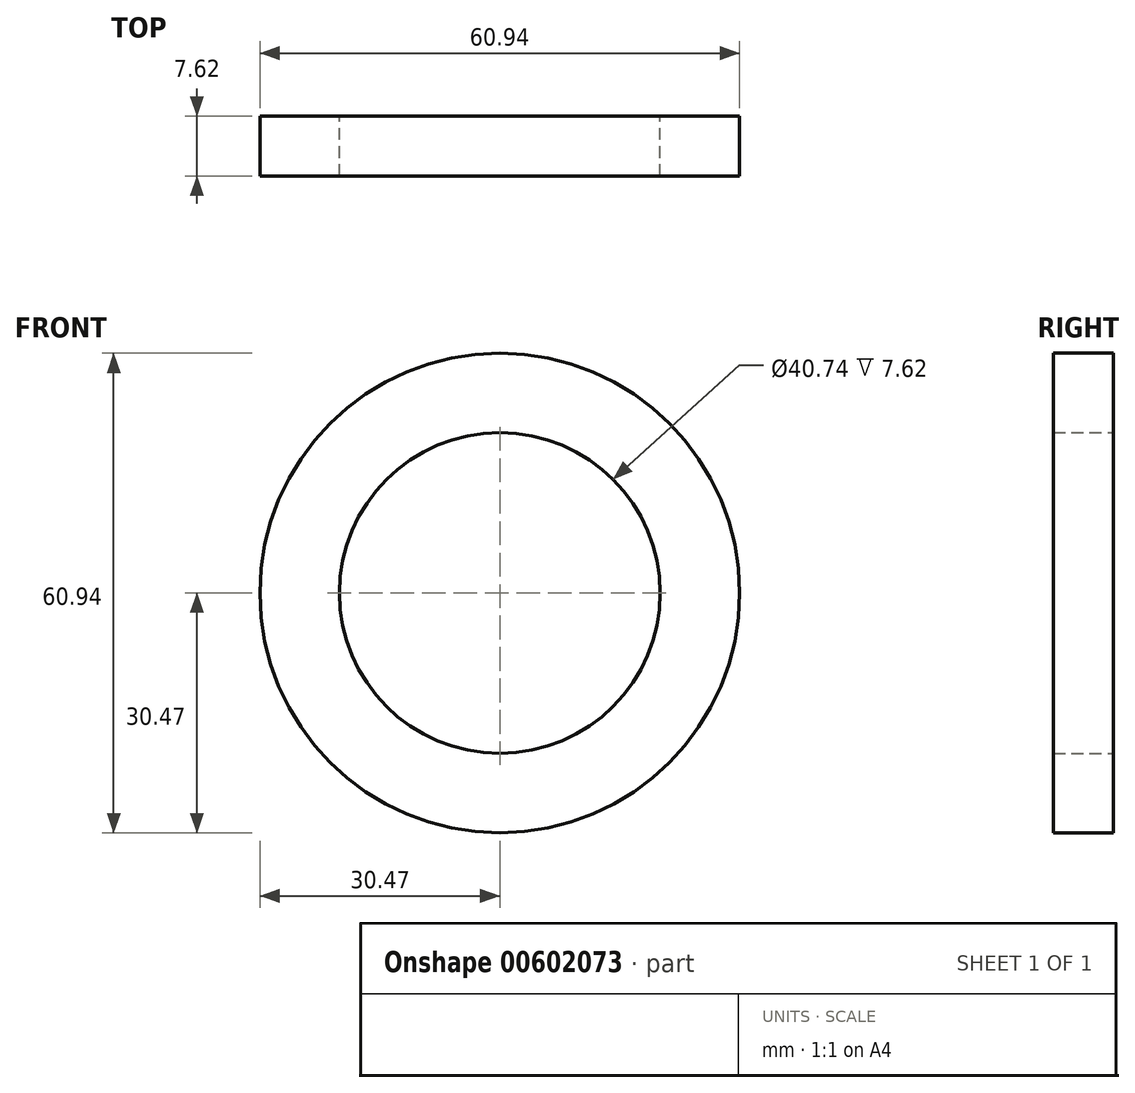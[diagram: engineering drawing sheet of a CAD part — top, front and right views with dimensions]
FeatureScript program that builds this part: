
annotation { "Feature Type Name" : "Feature", "Feature Type Description" : "" }
export const myFeature = defineFeature(function(context is Context, id is Id, definition is map)
    precondition{}
    {
        {
            var Q0;
            Q0=qCreatedBy(makeId("Front.planeOp"),FACE);
            var sketch = newSketch(context, id + "F0", { "sketchPlane" : qUnion([Q0])});
            skCircle(sketch, "E0", {"center": v(0, 0) * mm, "radius": 30.47 * mm});
            skCircle(sketch, "E1", {"center": v(0, 0) * mm, "radius": 20.37 * mm});
            skSolve(sketch);
        }
        {
            var Q0;
            Q0=makeQuery(id+"F0.imprint","IMPRINT",FACE,{"disambiguationData":[TD([[makeQuery(id+"F0.imprint","IMPRINT",EDGE,{"derivedFrom":sQuery(id+"F0.wireOp",EDGE,"E0")}),1.0]])]});
            extrude(context, id + "F1", {"entities" : qUnion([Q0]), "depth" : 7.62 * mm, "offsetDistance" : 25.4 * mm});
        }
    });
